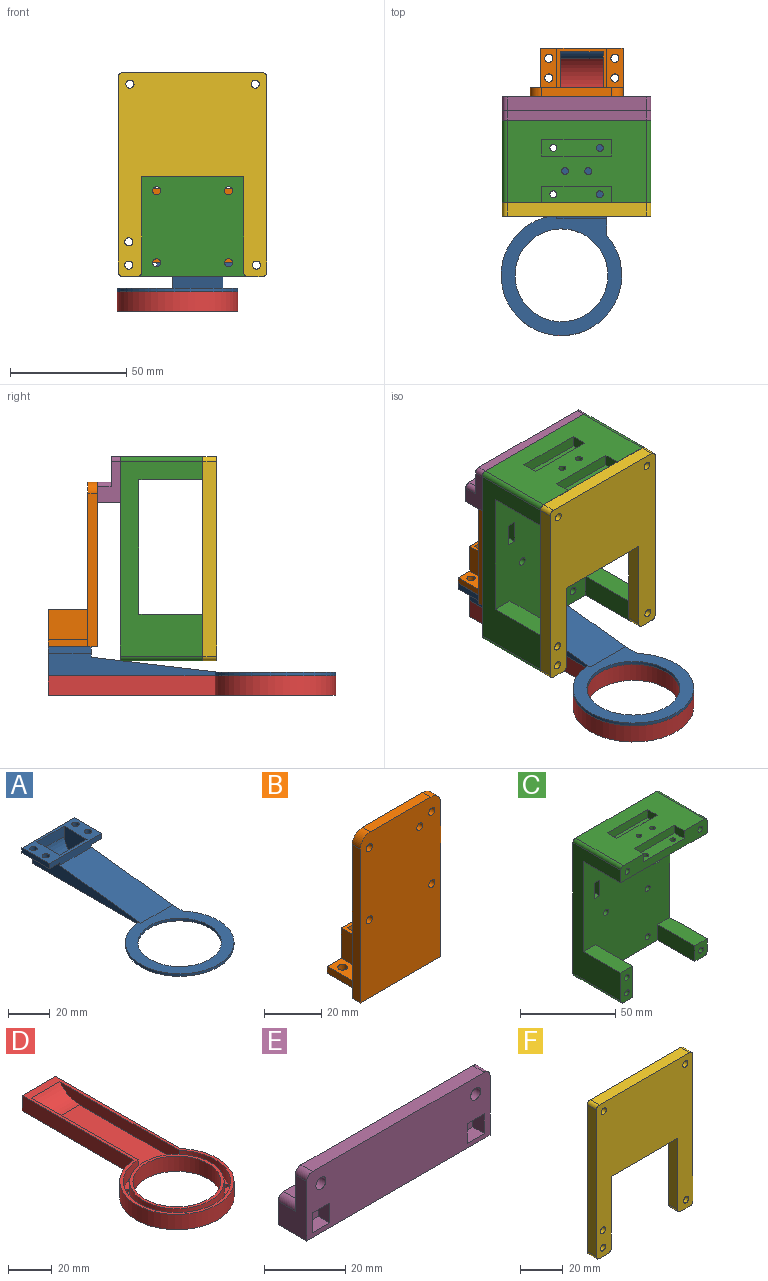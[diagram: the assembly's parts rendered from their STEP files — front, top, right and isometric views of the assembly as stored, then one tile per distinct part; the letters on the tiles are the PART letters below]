
ASSEMBLY  parts=6 mates=5
PART A: 26 faces, bbox 52.5x123.8x12.5 mm
  f0: plane 73.24x9.5mm, normal (-1,0,0), area 433.3mm2, adj f3,f8,f12,f15,f22,f23,f25
  f1: plane 54.84x18.52mm, normal (0,0.12,-0.99), area 1021.1mm2, adj f5,f6,f7,f21
  f2: plane 80.58x9.5mm, normal (1,0,0), area 446.5mm2, adj f3,f8,f12,f13,f22,f23,f25
  f3: cylinder r=26mm len=52mm, axis (0,0,-1), area 208.9mm2, adj f0,f2,f23,f25
  f4: cylinder r=20mm len=40mm, axis (0,0,-1), area 188.5mm2, adj f23,f24
  f5: plane 70.32x12.5mm, normal (-1,0,0), area 364mm2, adj f1,f7,f9,f10,f11,f25
  f6: plane 70.25x12.5mm, normal (1,0,0), area 364mm2, adj f1,f7,f9,f10,f11,f25
  f7: plane 18.5x6.02mm, normal (0,1,0), area 111.4mm2, adj f1,f5,f6,f11
  f8: plane 35.5x12.5mm, normal (0,1,0), area 310.8mm2, adj f0,f2,f11,f13,f14,f15,f16,f25
  f9: cylinder r=16mm len=18.5mm, axis (1,0,0), area 132.3mm2, adj f5,f6,f10,f25
  f10: plane 18.5x6mm, normal (0,-1,0), area 111mm2, adj f5,f6,f9,f11
  f11: plane 35.5x18.5mm, normal (0,0,1), area 331.5mm2, adj f5,f6,f7,f8,f10,f12,f14,f16
  f12: plane 35.5x4.52mm, normal (0,-1,0), area 139.2mm2, adj f0,f2,f11,f13,f14,f15,f16,f22
  f13: plane 18.5x7mm, normal (0,0,-1), area 110.3mm2, adj f2,f8,f12,f14,f17,f18
  f14: plane 18.5x3mm, normal (1,0,0), area 55.5mm2, adj f8,f11,f12,f13
  f15: plane 18.5x7mm, normal (0,0,-1), area 110.3mm2, adj f0,f8,f12,f16,f19,f20
  f16: plane 18.5x3mm, normal (-1,0,0), area 55.5mm2, adj f8,f11,f12,f15
  f17: cylinder r=1.75mm len=3.5mm, axis (0,0,-1), area 33mm2, adj f11,f13
  f18: cylinder r=1.75mm len=3.5mm, axis (0,0,-1), area 33mm2, adj f11,f13
  f19: cylinder r=1.75mm len=3.5mm, axis (0,0,-1), area 33mm2, adj f11,f15
  f20: cylinder r=1.75mm len=3.5mm, axis (0,0,-1), area 33mm2, adj f11,f15
  f21: plane 50.53x49.02mm, normal (0,0,-1), area 504mm2, adj f1,f24,f25
  f22: plane 54.84x21.52mm, normal (0,-0.12,0.99), area 1186.8mm2, adj f0,f2,f12,f23
  f23: plane 52.02x51.94mm, normal (0,0,1), area 886.2mm2, adj f0,f2,f3,f4,f22
  f24: plane 43x43mm, normal (0,0,-1), area 195.6mm2, adj f4,f21
  f25: plane 123.75x52mm, normal (0,0,-1), area 514.8mm2, adj f0,f2,f3,f5,f6,f8,f9,f21
PART B: 27 faces, bbox 40x21x71 mm
  f0: plane 66x4mm, normal (-1,0,0), area 264mm2, adj f1,f2,f3,f24
  f1: plane 40x21mm, normal (0,0,-1), area 438.3mm2, adj f0,f2,f3,f6,f13,f14,f15,f16
  f2: plane 71x40mm, normal (0,-1,0), area 2792mm2, adj f0,f1,f5,f6,f7,f8,f9,f10
  f3: plane 71x40mm, normal (0,1,0), area 2702mm2, adj f0,f1,f4,f5,f6,f7,f8,f9
  f4: plane 17x13mm, normal (1,0,0), area 221mm2, adj f3,f12,f13,f17
  f5: plane 30x4mm, normal (0,0,1), area 120mm2, adj f2,f3,f24,f25
  f6: plane 66x21mm, normal (1,0,0), area 315mm2, adj f1,f2,f3,f13,f17,f25
  f7: cylinder r=1.55mm len=4mm, axis (0,-1,0), area 39mm2, adj f2,f3
  f8: cylinder r=1.55mm len=4mm, axis (0,-1,0), area 39mm2, adj f2,f3
  f9: cylinder r=1.55mm len=4mm, axis (0,-1,0), area 39mm2, adj f2,f3
  f10: cylinder r=1.55mm len=4mm, axis (0,-1,0), area 39mm2, adj f2,f3
  f11: plane 17x13mm, normal (-1,0,0), area 221mm2, adj f3,f12,f13,f18
  f12: plane 21.5x17mm, normal (0,0,1), area 78.8mm2, adj f3,f4,f11,f13,f14,f15,f16
  f13: plane 35.5x16mm, normal (0,1,0), area 386mm2, adj f1,f4,f6,f11,f12,f17,f18,f19
  f14: plane 16x15.5mm, normal (-1,0,0), area 248mm2, adj f1,f3,f12,f16
  f15: plane 16x15.5mm, normal (1,0,0), area 248mm2, adj f1,f3,f12,f16
  f16: plane 18.5x16mm, normal (0,-1,0), area 296mm2, adj f1,f12,f14,f15
  f17: plane 17x7mm, normal (0,0,1), area 99.8mm2, adj f3,f4,f6,f13,f22,f23
  f18: plane 17x7mm, normal (0,0,1), area 99.8mm2, adj f3,f11,f13,f19,f20,f21
  f19: plane 17x3mm, normal (-1,0,0), area 51mm2, adj f1,f3,f13,f18
  f20: cylinder r=1.75mm len=3.5mm, axis (0,0,1), area 33mm2, adj f1,f18
  f21: cylinder r=1.75mm len=3.5mm, axis (0,0,1), area 33mm2, adj f1,f18
  f22: cylinder r=1.75mm len=3.5mm, axis (0,0,1), area 33mm2, adj f1,f17
  f23: cylinder r=1.75mm len=3.5mm, axis (0,0,1), area 33mm2, adj f1,f17
  f24: cylinder r=5mm len=5mm, axis (0,-1,0), area 31.4mm2, adj f0,f2,f3,f5
  f25: cylinder r=5mm len=5mm, axis (0,1,0), area 31.4mm2, adj f2,f3,f5,f6
  f26: cylinder r=1.5mm len=4mm, axis (0,-1,0), area 37.7mm2, adj f2,f3
PART C: 60 faces, bbox 64x35.5x88 mm
  f0: plane 88x64mm, normal (0,1,0), area 5462mm2, adj f5,f11,f12,f13,f14,f15,f18,f19
  f1: plane 78x64mm, normal (0,-1,0), area 4603.5mm2, adj f2,f11,f12,f13,f16,f17,f21,f22
  f2: plane 64x27.5mm, normal (0,0,-1), area 1659.7mm2, adj f1,f6,f7,f8,f9,f10,f11,f13
  f3: cylinder r=1.5mm len=7mm, axis (0,0,1), area 66mm2, adj f5,f39
  f4: cylinder r=1.5mm len=7mm, axis (0,0,1), area 66mm2, adj f5,f34
  f5: plane 60x35.5mm, normal (0,0,1), area 1695.9mm2, adj f0,f3,f4,f6,f26,f27,f28,f29
  f6: plane 64x10mm, normal (0,-1,0), area 469mm2, adj f2,f5,f11,f13,f14,f15,f30,f31
  f7: cylinder r=1.5mm len=5mm, axis (0,0,1), area 47.1mm2, adj f2,f25
  f8: cylinder r=1.5mm len=5mm, axis (0,0,1), area 47.1mm2, adj f2,f30
  f9: cylinder r=1.5mm len=5mm, axis (0,0,1), area 47.1mm2, adj f2,f30
  f10: cylinder r=1.5mm len=5mm, axis (0,0,1), area 47.1mm2, adj f2,f25
  f11: plane 84x35.5mm, normal (-1,0,0), area 1387mm2, adj f0,f1,f2,f6,f17,f20,f56,f57
  f12: plane 60x35.5mm, normal (0,0,-1), area 865mm2, adj f0,f1,f16,f20,f22,f24,f57,f58
  f13: plane 84x35.5mm, normal (1,0,0), area 1112mm2, adj f0,f1,f2,f6,f21,f24,f58,f59
  f14: cylinder r=1.75mm len=35.5mm, axis (0,1,0), area 390.3mm2, adj f0,f6
  f15: cylinder r=1.75mm len=35.5mm, axis (0,1,0), area 390.3mm2, adj f0,f6
  f16: plane 27.5x20mm, normal (1,0,0), area 550mm2, adj f1,f12,f17,f20
  f17: plane 27.5x9mm, normal (0,0,1), area 247.5mm2, adj f1,f11,f16,f20
  f18: cylinder r=1.75mm len=35.5mm, axis (0,1,0), area 390.3mm2, adj f0,f20
  f19: cylinder r=1.75mm len=35.5mm, axis (0,1,0), area 390.3mm2, adj f0,f20
  f20: plane 20x9mm, normal (0,-1,0), area 159.9mm2, adj f11,f12,f16,f17,f18,f19,f57
  f21: plane 27.5x9mm, normal (0,0,1), area 247.5mm2, adj f1,f13,f22,f24
  f22: plane 27.5x10mm, normal (-1,0,0), area 275mm2, adj f1,f12,f21,f24
  f23: cylinder r=1.75mm len=35.5mm, axis (0,1,0), area 390.3mm2, adj f0,f24
  f24: plane 10x9mm, normal (0,-1,0), area 79.5mm2, adj f12,f13,f21,f22,f23,f58
  f25: plane 30x7mm, normal (0,0,1), area 195.9mm2, adj f7,f10,f26,f27,f28,f29
  f26: plane 7x5mm, normal (1,0,0), area 35mm2, adj f5,f25,f27,f29
  f27: plane 30x5mm, normal (0,1,0), area 150mm2, adj f5,f25,f26,f28
  f28: plane 7x5mm, normal (-1,0,0), area 35mm2, adj f5,f25,f27,f29
  f29: plane 30x5mm, normal (0,-1,0), area 150mm2, adj f5,f25,f26,f28
  f30: plane 30x7mm, normal (0,0,1), area 195.9mm2, adj f6,f8,f9,f31,f32,f33
  f31: plane 7x5mm, normal (-1,0,0), area 35mm2, adj f5,f6,f30,f32
  f32: plane 30x5mm, normal (0,-1,0), area 150mm2, adj f5,f30,f31,f33
  f33: plane 7x5mm, normal (1,0,0), area 35mm2, adj f5,f6,f30,f32
  f34: plane 6x6mm, normal (0,0,-1), area 28.9mm2, adj f4,f35,f36,f37,f38
  f35: plane 6x3mm, normal (1,0,0), area 18mm2, adj f2,f34,f36,f38
  f36: plane 6x3mm, normal (0,-1,0), area 18mm2, adj f2,f34,f35,f37
  f37: plane 6x3mm, normal (-1,0,0), area 18mm2, adj f2,f34,f36,f38
  f38: plane 6x3mm, normal (0,1,0), area 18mm2, adj f2,f34,f35,f37
  f39: plane 6x6mm, normal (0,0,-1), area 28.9mm2, adj f3,f40,f41,f42,f43
  f40: plane 6x3mm, normal (0,-1,0), area 18mm2, adj f2,f39,f41,f43
  f41: plane 6x3mm, normal (-1,0,0), area 18mm2, adj f2,f39,f40,f42
  f42: plane 6x3mm, normal (0,1,0), area 18mm2, adj f2,f39,f41,f43
  f43: plane 6x3mm, normal (1,0,0), area 18mm2, adj f2,f39,f40,f42
  f44: cylinder r=1.75mm len=8mm, axis (0,-1,0), area 88mm2, adj f0,f1
  f45: cylinder r=1.75mm len=8mm, axis (0,-1,0), area 88mm2, adj f0,f1
  f46: cylinder r=1.75mm len=8mm, axis (0,-1,0), area 88mm2, adj f0,f1
  f47: cylinder r=1.75mm len=8mm, axis (0,-1,0), area 88mm2, adj f0,f1
  f48: plane 10x8mm, normal (-1,0,0), area 80mm2, adj f0,f1,f49,f51
  f49: plane 8x4mm, normal (0,0,-1), area 32mm2, adj f0,f1,f48,f50
  f50: plane 10x8mm, normal (1,0,0), area 80mm2, adj f0,f1,f49,f51
  f51: plane 8x4mm, normal (0,0,1), area 32mm2, adj f0,f1,f48,f50
  f52: plane 8x4mm, normal (0,0,-1), area 32mm2, adj f0,f1,f53,f55
  f53: plane 10x8mm, normal (1,0,0), area 80mm2, adj f0,f1,f52,f54
  f54: plane 8x4mm, normal (0,0,1), area 32mm2, adj f0,f1,f53,f55
  f55: plane 10x8mm, normal (-1,0,0), area 80mm2, adj f0,f1,f52,f54
  f56: cylinder r=2mm len=35.5mm, axis (0,-1,0), area 111.5mm2, adj f0,f5,f6,f11
  f57: cylinder r=2mm len=35.5mm, axis (0,1,0), area 111.5mm2, adj f0,f11,f12,f20
  f58: cylinder r=2mm len=35.5mm, axis (0,-1,0), area 111.5mm2, adj f0,f12,f13,f24
  f59: cylinder r=2mm len=35.5mm, axis (0,1,0), area 111.5mm2, adj f0,f5,f6,f13
PART D: 32 faces, bbox 52x123.7x8.5 mm
  f0: plane 43x43mm, normal (0,0,1), area 195.6mm2, adj f18,f30
  f1: cylinder r=1.25mm len=2.5mm, axis (0,0,-1), area 15.7mm2, adj f19,f29
  f2: cylinder r=1.25mm len=2.5mm, axis (0,0,-1), area 15.7mm2, adj f19,f29
  f3: cylinder r=1.25mm len=2.5mm, axis (0,0,-1), area 15.7mm2, adj f19,f29
  f4: cylinder r=1.25mm len=2.5mm, axis (0,0,-1), area 15.7mm2, adj f19,f29
  f5: cylinder r=1.25mm len=2.5mm, axis (0,0,-1), area 15.7mm2, adj f19,f29
  f6: cylinder r=1.25mm len=2.5mm, axis (0,0,-1), area 15.7mm2, adj f19,f29
  f7: cylinder r=1.25mm len=2.5mm, axis (0,0,-1), area 15.7mm2, adj f19,f29
  f8: cylinder r=1.25mm len=2.5mm, axis (0,0,-1), area 15.7mm2, adj f19,f29
  f9: cylinder r=1.25mm len=2.5mm, axis (0,0,-1), area 15.7mm2, adj f19,f29
  f10: cylinder r=1.25mm len=2.5mm, axis (0,0,-1), area 15.7mm2, adj f19,f29
  f11: cylinder r=1.25mm len=2.5mm, axis (0,0,-1), area 15.7mm2, adj f19,f29
  f12: cylinder r=1.25mm len=2.5mm, axis (0,0,-1), area 15.7mm2, adj f19,f29
  f13: cylinder r=1.25mm len=2.5mm, axis (0,0,-1), area 15.7mm2, adj f19,f29
  f14: cylinder r=1.25mm len=2.5mm, axis (0,0,-1), area 15.7mm2, adj f19,f29
  f15: cylinder r=1.25mm len=2.5mm, axis (0,0,-1), area 15.7mm2, adj f19,f29
  f16: cylinder r=1.25mm len=2.5mm, axis (0,0,-1), area 15.7mm2, adj f19,f29
  f17: cylinder r=1.25mm len=2.5mm, axis (0,0,-1), area 15.7mm2, adj f19,f29
  f18: cylinder r=20mm len=40mm, axis (0,0,-1), area 1068.1mm2, adj f0,f19
  f19: plane 123.75x52mm, normal (0,0,-1), area 2374.2mm2, adj f1,f2,f3,f4,f5,f6,f7,f8
  f20: cylinder r=26mm len=52mm, axis (0,0,-1), area 1184mm2, adj f19,f22,f23,f31
  f21: plane 21.5x8.5mm, normal (0,1,0), area 182.8mm2, adj f19,f22,f23,f31
  f22: plane 80.58x8.5mm, normal (1,0,0), area 684.9mm2, adj f19,f20,f21,f31
  f23: plane 71.82x8.5mm, normal (-1,0,0), area 610.5mm2, adj f19,f20,f21,f31
  f24: cylinder r=1.25mm len=2.5mm, axis (0,0,-1), area 15.7mm2, adj f19,f29
  f25: plane 68.91x6.5mm, normal (1,0,0), area 422.8mm2, adj f26,f28,f29,f31
  f26: cylinder r=24.5mm len=49mm, axis (0,0,-1), area 865.8mm2, adj f25,f27,f29,f31
  f27: plane 76.81x6.5mm, normal (-1,0,0), area 474.1mm2, adj f26,f28,f29,f31
  f28: cylinder r=16mm len=18.5mm, axis (1,0,0), area 276.8mm2, adj f25,f27,f29,f31
  f29: plane 105.03x49mm, normal (0,0,1), area 1425.7mm2, adj f1,f2,f3,f4,f5,f6,f7,f8
  f30: cylinder r=21.5mm len=43mm, axis (0,0,-1), area 878.1mm2, adj f0,f29
  f31: plane 123.75x52mm, normal (0,0,1), area 514.8mm2, adj f20,f21,f22,f23,f25,f26,f27,f28
PART E: 26 faces, bbox 64x10x20 mm
  f0: cylinder r=1.75mm len=6mm, axis (0,1,0), area 66mm2, adj f13,f19
  f1: cylinder r=1.75mm len=6mm, axis (0,1,0), area 66mm2, adj f13,f14
  f2: plane 18x10mm, normal (-1,0,0), area 114mm2, adj f7,f8,f10,f11,f13,f25
  f3: plane 18x10mm, normal (1,0,0), area 114mm2, adj f7,f8,f9,f11,f13,f24
  f4: cylinder r=1.75mm len=4mm, axis (0,1,0), area 44mm2, adj f7,f8
  f5: cylinder r=1.75mm len=4mm, axis (0,1,0), area 44mm2, adj f7,f8
  f6: plane 60x4mm, normal (0,0,1), area 240mm2, adj f7,f8,f9,f10
  f7: plane 64x20mm, normal (0,-1,0), area 1187mm2, adj f2,f3,f4,f5,f6,f9,f10,f11
  f8: plane 64x13mm, normal (0,1,0), area 684.8mm2, adj f2,f3,f4,f5,f6,f9,f10,f12
  f9: cylinder r=2mm len=4mm, axis (0,1,0), area 12.6mm2, adj f3,f6,f7,f8
  f10: cylinder r=2mm len=4mm, axis (0,-1,0), area 12.6mm2, adj f2,f6,f7,f8
  f11: plane 64x10mm, normal (0,0,-1), area 640mm2, adj f2,f3,f7,f13
  f12: plane 60x6mm, normal (0,0,1), area 360mm2, adj f8,f13,f24,f25
  f13: plane 64x9mm, normal (0,1,0), area 555mm2, adj f0,f1,f2,f3,f11,f12,f24,f25
  f14: plane 6x6mm, normal (0,-1,0), area 26.4mm2, adj f1,f15,f16,f17,f18
  f15: plane 6x4mm, normal (1,0,0), area 24mm2, adj f7,f14,f16,f18
  f16: plane 6x4mm, normal (0,0,1), area 24mm2, adj f7,f14,f15,f17
  f17: plane 6x4mm, normal (-1,0,0), area 24mm2, adj f7,f14,f16,f18
  f18: plane 6x4mm, normal (0,0,-1), area 24mm2, adj f7,f14,f15,f17
  f19: plane 6x6mm, normal (0,-1,0), area 26.4mm2, adj f0,f20,f21,f22,f23
  f20: plane 6x4mm, normal (1,0,0), area 24mm2, adj f7,f19,f21,f23
  f21: plane 6x4mm, normal (0,0,1), area 24mm2, adj f7,f19,f20,f22
  f22: plane 6x4mm, normal (-1,0,0), area 24mm2, adj f7,f19,f21,f23
  f23: plane 6x4mm, normal (0,0,-1), area 24mm2, adj f7,f19,f20,f22
  f24: cylinder r=2mm len=6mm, axis (0,-1,0), area 18.8mm2, adj f3,f8,f12,f13
  f25: cylinder r=2mm len=6mm, axis (0,1,0), area 18.8mm2, adj f2,f8,f12,f13
PART F: 21 faces, bbox 64x6x88 mm
  f0: plane 6x6mm, normal (0,0,-1), area 36mm2, adj f5,f6,f15,f19
  f1: plane 60x6mm, normal (0,0,1), area 360mm2, adj f5,f6,f17,f20
  f2: plane 84x6mm, normal (-1,0,0), area 504mm2, adj f5,f6,f17,f18
  f3: plane 6x6mm, normal (0,0,-1), area 36mm2, adj f5,f6,f16,f18
  f4: plane 84x6mm, normal (1,0,0), area 504mm2, adj f5,f6,f19,f20
  f5: plane 88x64mm, normal (0,-1,0), area 3686.7mm2, adj f0,f1,f2,f3,f4,f7,f8,f9
  f6: plane 88x64mm, normal (0,1,0), area 3686.7mm2, adj f0,f1,f2,f3,f4,f7,f8,f9
  f7: cylinder r=1.75mm len=6mm, axis (0,-1,0), area 66mm2, adj f5,f6
  f8: cylinder r=1.75mm len=6mm, axis (0,-1,0), area 66mm2, adj f5,f6
  f9: plane 44x6mm, normal (0,0,-1), area 264mm2, adj f5,f6,f10,f11
  f10: plane 41x6mm, normal (1,0,0), area 246mm2, adj f5,f6,f9,f16
  f11: plane 41x6mm, normal (-1,0,0), area 246mm2, adj f5,f6,f9,f15
  f12: cylinder r=1.75mm len=6mm, axis (0,-1,0), area 66mm2, adj f5,f6
  f13: cylinder r=1.75mm len=6mm, axis (0,-1,0), area 66mm2, adj f5,f6
  f14: cylinder r=1.75mm len=6mm, axis (0,-1,0), area 66mm2, adj f5,f6
  f15: cylinder r=2mm len=6mm, axis (0,1,0), area 18.8mm2, adj f0,f5,f6,f11
  f16: cylinder r=2mm len=6mm, axis (0,-1,0), area 18.8mm2, adj f3,f5,f6,f10
  f17: cylinder r=2mm len=6mm, axis (0,-1,0), area 18.8mm2, adj f1,f2,f5,f6
  f18: cylinder r=2mm len=6mm, axis (0,1,0), area 18.8mm2, adj f2,f3,f5,f6
  f19: cylinder r=2mm len=6mm, axis (0,-1,0), area 18.8mm2, adj f0,f4,f5,f6
  f20: cylinder r=2mm len=6mm, axis (0,1,0), area 18.8mm2, adj f1,f4,f5,f6
PLACE A t=(47.54,105.87,-62.66)mm
PLACE B t=(46.18,146.64,-6.16)mm
PLACE C t=(46.18,132.64,-3.66)mm
PLACE D t=(47.54,105.87,-62.66)mm
PLACE E t=(46.18,136.64,35.34)mm
PLACE F t=(46.18,97.14,-3.66)mm
MATE fastened B.f2 <-> E.f13  axis (0,-1,0) through (46.18,142.64,29.34)mm
MATE fastened D.f31 <-> A.f25  axis (0,0,1) through (37.68,163.64,-54.16)mm
MATE fastened E.f7 <-> C.f0  axis (0,-1,0) through (46.18,132.64,40.34)mm
MATE fastened F.f20 <-> C.f59  axis (0,1,0) through (76.18,97.14,38.34)mm
MATE fastened B.f1 <-> A.f11  axis (0,0,1) through (66.18,163.64,-41.66)mm
